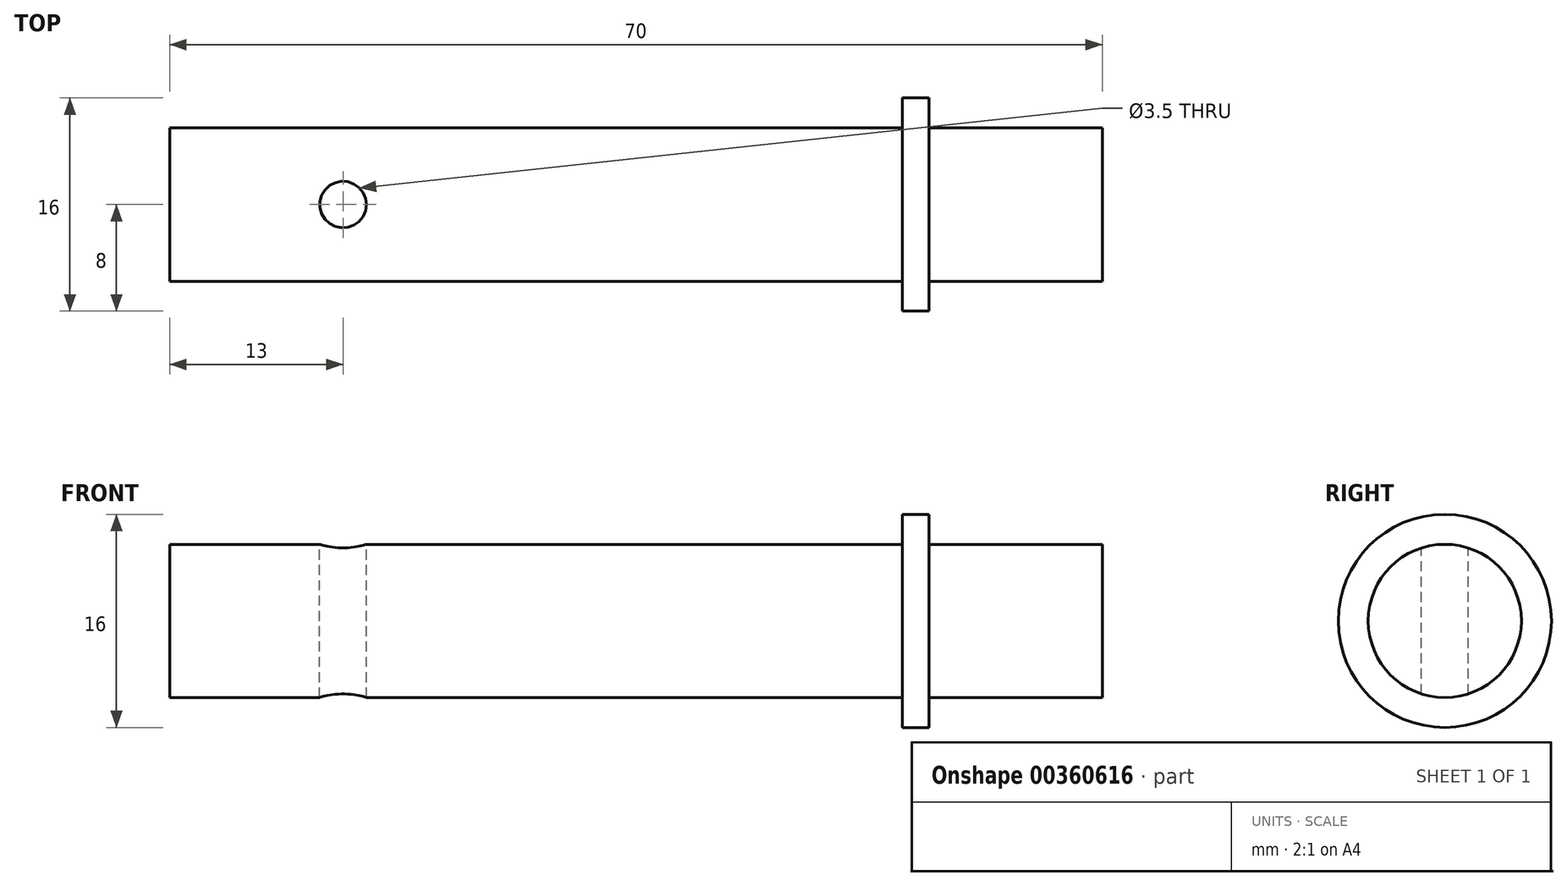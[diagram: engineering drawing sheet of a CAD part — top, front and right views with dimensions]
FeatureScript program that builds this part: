
annotation { "Feature Type Name" : "Feature", "Feature Type Description" : "" }
export const myFeature = defineFeature(function(context is Context, id is Id, definition is map)
    precondition{}
    {
        {
            var Q0;
            Q0=qCreatedBy(makeId("Right.planeOp"),FACE);
            var sketch = newSketch(context, id + "F0", { "sketchPlane" : qUnion([Q0])});
            skCircle(sketch, "E0", {"center": v(0, 0) * mm, "radius": 5.75 * mm});
            skSolve(sketch);
        }
        {
            var Q0;
            Q0 = qSketchRegion(id + "F0", true);
            extrude(context, id + "F1", {"entities" : qUnion([Q0]), "depth" : 70 * mm});
        }
        {
            var Q0;
            Q0=qCreatedBy(makeId("Top.planeOp"),FACE);
            cPlane(context, id + "F2", {"entities" : qUnion([Q0]), "cplaneType" : CPlaneType.OFFSET, "offset" : 6.8 * mm, "width" : 150 * mm, "height" : 150 * mm});
        }
        {
            var Q0;
            Q0=qCreatedBy(id+"F2.planeOp",FACE);
            var sketch = newSketch(context, id + "F3", { "sketchPlane" : qUnion([Q0])});
            skLineSegment(sketch, "E1", {"start": v(0, 0) * mm, "end": v(70, 0) * mm});
            skLineSegment(sketch, "E2", {"start": v(0, 0) * mm, "end": v(13, 0) * mm});
            skCircle(sketch, "E3", {"center": v(13, 0) * mm, "radius": 1.75 * mm});
            skLineSegment(sketch, "E4", {"start": v(70, 0) * mm, "end": v(55, 0) * mm});
            skSolve(sketch);
        }
        {
            var Q0;
            Q0 = qSketchRegion(id + "F3", true);
            extrude(context, id + "F4", {"entities" : qUnion([Q0]), "operationType" : NewBodyOperationType.REMOVE, "oppositeDirection" : true, "depth" : 25 * mm});
        }
        {
            var Q0;
            Q0=qCreatedBy(makeId("Right.planeOp"),FACE);
            cPlane(context, id + "F5", {"entities" : qUnion([Q0]), "cplaneType" : CPlaneType.OFFSET, "offset" : 55 * mm, "width" : 150 * mm, "height" : 150 * mm});
        }
        {
            var Q0;
            Q0=qCreatedBy(id+"F5.planeOp",FACE);
            var sketch = newSketch(context, id + "F6", { "sketchPlane" : qUnion([Q0])});
            skCircle(sketch, "E5", {"center": v(0, 0) * mm, "radius": 8 * mm});
            skSolve(sketch);
        }
        {
            var Q0;
            Q0 = qSketchRegion(id + "F6", true);
            extrude(context, id + "F7", {"entities" : qUnion([Q0]), "operationType" : NewBodyOperationType.ADD, "depth" : 2 * mm});
        }
    });
